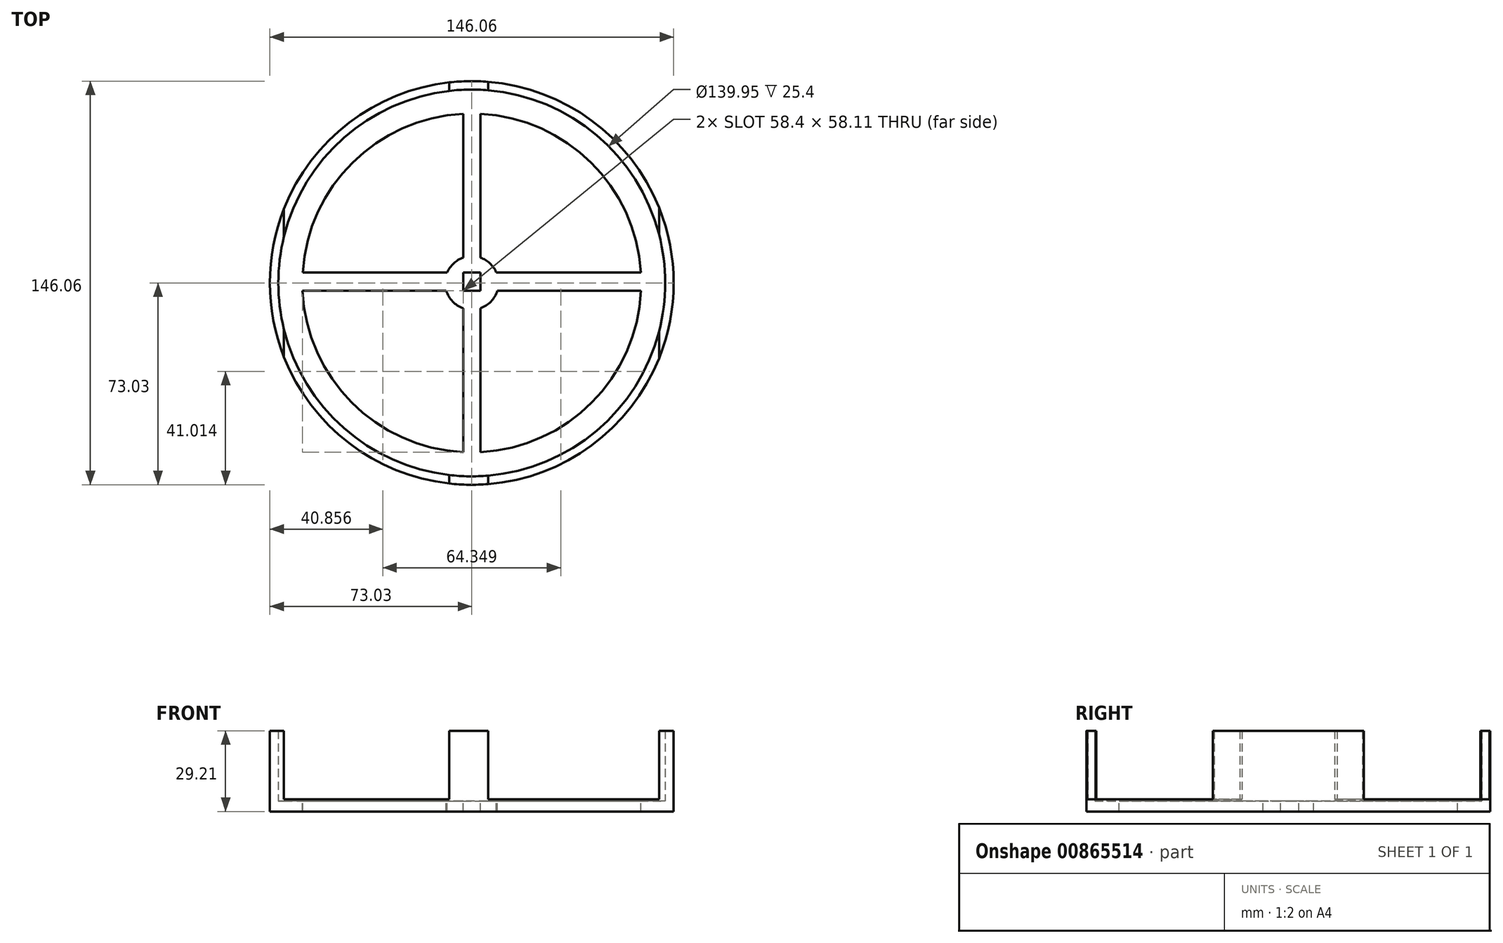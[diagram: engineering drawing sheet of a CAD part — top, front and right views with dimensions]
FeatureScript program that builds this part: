
annotation { "Feature Type Name" : "Feature", "Feature Type Description" : "" }
export const myFeature = defineFeature(function(context is Context, id is Id, definition is map)
    precondition{}
    {
        {
            var Q0;
            Q0=qCreatedBy(makeId("Top.planeOp"),FACE);
            var sketch = newSketch(context, id + "F0", { "sketchPlane" : qUnion([Q0])});
            skCircle(sketch, "E0", {"center": v(0, 0) * mm, "radius": 73.03 * mm});
            skSolve(sketch);
        }
        {
            var Q0;
            Q0=makeQuery(id+"F0.imprint","IMPRINT",FACE,{"disambiguationData":[TD([[makeQuery(id+"F0.imprint","IMPRINT",EDGE,{"derivedFrom":sQuery(id+"F0.wireOp",EDGE,"E0")}),1.0]])]});
            extrude(context, id + "F1", {"entities" : qUnion([Q0]), "depth" : 3.8 * mm, "offsetDistance" : 25.4 * mm});
        }
        {
            var Q0;
            Q0=makeQuery(id+"F1.opExtrude","CAP_FACE",FACE,{"disambiguationData":[OSD([sQuery(id+"F0.wireOp",EDGE,"E0")])],"isStart":false});
            var sketch = newSketch(context, id + "F2", { "sketchPlane" : qUnion([Q0])});
            skCircle(sketch, "E1", {"center": v(0, 0) * mm, "radius": 69.98 * mm});
            skSolve(sketch);
        }
        {
            var Q0;
            Q0=makeQuery(id+"F2.imprint","IMPRINT",FACE,{"disambiguationData":[TD([[makeQuery(id+"F2.imprint","IMPRINT",EDGE,{"derivedFrom":sQuery(id+"F2.wireOp",EDGE,"E1")}),-1.0]])]});
            extrude(context, id + "F3", {"entities" : qUnion([Q0]), "operationType" : NewBodyOperationType.ADD, "depth" : 25.4 * mm, "offsetDistance" : 25.4 * mm});
        }
        {
            var Q0;
            Q0=makeQuery(id+"F1.opExtrude","CAP_FACE",FACE,{"disambiguationData":[OSD([sQuery(id+"F0.wireOp",EDGE,"E0")])],"isStart":false});
            var sketch = newSketch(context, id + "F4", { "sketchPlane" : qUnion([Q0])});
            skCircle(sketch, "E2", {"center": v(0, 0) * mm, "radius": 61.3 * mm});
            skSolve(sketch);
        }
        {
            var Q0;
            Q0=makeQuery(id+"F4.imprint","IMPRINT",FACE,{"disambiguationData":[TD([[makeQuery(id+"F4.imprint","IMPRINT",EDGE,{"derivedFrom":sQuery(id+"F4.wireOp",EDGE,"E2")}),1.0]])]});
            extrude(context, id + "F5", {"entities" : qUnion([Q0]), "operationType" : NewBodyOperationType.REMOVE, "oppositeDirection" : true, "depth" : 25.4 * mm, "offsetDistance" : 25.4 * mm});
        }
        {
            var Q0;
            Q0=makeQuery(id+"F1.opExtrude","CAP_FACE",FACE,{"disambiguationData":[OSD([sQuery(id+"F0.wireOp",EDGE,"E0")])],"isStart":false});
            var sketch = newSketch(context, id + "F6", { "sketchPlane" : qUnion([Q0])});
            skLineSegment(sketch, "E3.bottom", {"start": v(-3.12, 65.22) * mm, "end": v(3.12, 65.22) * mm});
            skLineSegment(sketch, "E3.top", {"start": v(-3.12, -64.2) * mm, "end": v(3.12, -64.2) * mm});
            skLineSegment(sketch, "E3.left", {"start": v(-3.12, 65.22) * mm, "end": v(-3.12, -64.2) * mm});
            skLineSegment(sketch, "E3.right", {"start": v(3.12, 65.22) * mm, "end": v(3.12, -64.2) * mm});
            skLineSegment(sketch, "E4.bottom", {"start": v(-63.3, 3.82) * mm, "end": v(64.1, 3.82) * mm});
            skLineSegment(sketch, "E4.top", {"start": v(-63.3, -2.82) * mm, "end": v(64.1, -2.82) * mm});
            skLineSegment(sketch, "E4.left", {"start": v(-63.3, 3.82) * mm, "end": v(-63.3, -2.82) * mm});
            skLineSegment(sketch, "E4.right", {"start": v(64.1, 3.82) * mm, "end": v(64.1, -2.82) * mm});
            skCircle(sketch, "E5", {"center": v(0, 0) * mm, "radius": 9.66 * mm});
            skSolve(sketch);
        }
        {
            var Q0;
            Q0 = qSketchRegion(id + "F6", true);
            var Q1;
            Q1=makeQuery(id+"F1.opExtrude","CAP_FACE",FACE,{"disambiguationData":[OSD([sQuery(id+"F0.wireOp",EDGE,"E0")])],"isStart":true});
            extrude(context, id + "F7", {"entities" : qUnion([Q0]), "operationType" : NewBodyOperationType.ADD, "endBound" : BoundingType.UP_TO_SURFACE, "oppositeDirection" : true, "depth" : 25.4 * mm, "endBoundEntityFace" : qUnion([Q1]), "offsetDistance" : 25.4 * mm});
        }
        {
            var Q0;
            Q0=qCreatedBy(makeId("Front.planeOp"),FACE);
            var sketch = newSketch(context, id + "F8", { "sketchPlane" : qUnion([Q0])});
            skLineSegment(sketch, "E6.bottom", {"start": v(-67.93, 33.82) * mm, "end": v(-8.15, 33.82) * mm});
            skLineSegment(sketch, "E6.top", {"start": v(-67.93, 4.43) * mm, "end": v(-8.15, 4.43) * mm});
            skLineSegment(sketch, "E6.left", {"start": v(-67.93, 33.82) * mm, "end": v(-67.93, 4.43) * mm});
            skLineSegment(sketch, "E6.right", {"start": v(-8.15, 33.82) * mm, "end": v(-8.15, 4.43) * mm});
            skLineSegment(sketch, "E7.bottom", {"start": v(5.94, 33.82) * mm, "end": v(67.73, 33.82) * mm});
            skLineSegment(sketch, "E7.top", {"start": v(5.94, 4.43) * mm, "end": v(67.73, 4.43) * mm});
            skLineSegment(sketch, "E7.left", {"start": v(5.94, 33.82) * mm, "end": v(5.94, 4.43) * mm});
            skLineSegment(sketch, "E7.right", {"start": v(67.73, 33.82) * mm, "end": v(67.73, 4.43) * mm});
            skSolve(sketch);
        }
        {
            var Q0;
            Q0 = qSketchRegion(id + "F8", true);
            extrude(context, id + "F9", {"entities" : qUnion([Q0]), "operationType" : NewBodyOperationType.REMOVE, "oppositeDirection" : true, "depth" : 254 * mm, "offsetDistance" : 25.4 * mm, "symmetric" : true});
        }
    });
